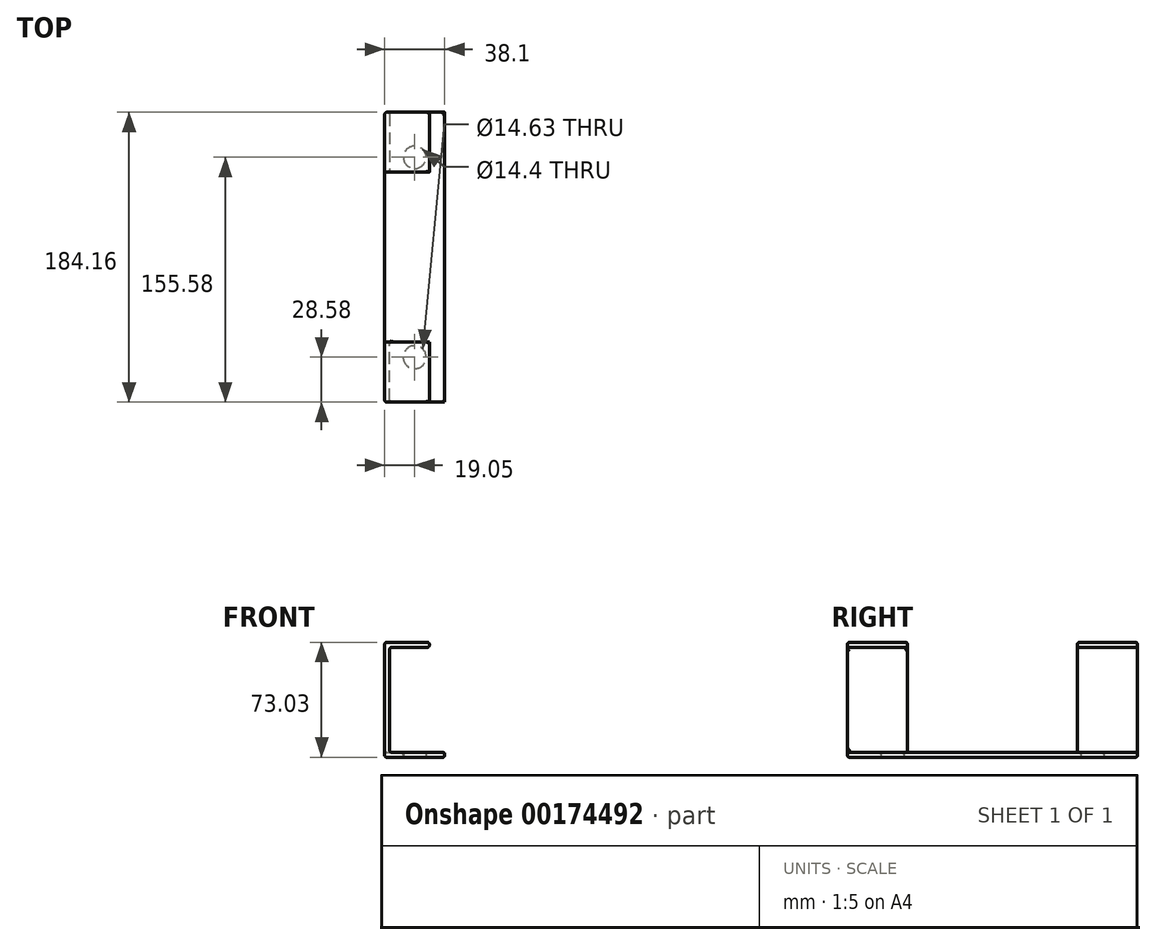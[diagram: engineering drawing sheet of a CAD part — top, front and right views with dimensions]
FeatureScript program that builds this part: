
annotation { "Feature Type Name" : "Feature", "Feature Type Description" : "" }
export const myFeature = defineFeature(function(context is Context, id is Id, definition is map)
    precondition{}
    {
        {
            var Q0;
            Q0=qCreatedBy(makeId("Top.planeOp"),FACE);
            var sketch = newSketch(context, id + "F0", { "sketchPlane" : qUnion([Q0])});
            skLineSegment(sketch, "E0.bottom", {"start": v(-19.05, -92.07) * mm, "end": v(19.05, -92.07) * mm});
            skLineSegment(sketch, "E0.top", {"start": v(-19.05, 92.08) * mm, "end": v(19.05, 92.08) * mm});
            skLineSegment(sketch, "E0.left", {"start": v(-19.05, -92.07) * mm, "end": v(-19.05, 92.08) * mm});
            skLineSegment(sketch, "E0.right", {"start": v(19.05, -92.07) * mm, "end": v(19.05, 92.08) * mm});
            skPoint(sketch, "E0.middle", {"position": v(0, 0) * mm});
            skCircle(sketch, "E1", {"center": v(0, -63.5) * mm, "radius": 7.32 * mm});
            skCircle(sketch, "E2", {"center": v(0, 63.5) * mm, "radius": 7.2 * mm});
            skSolve(sketch);
        }
        {
            var Q0;
            Q0=qSketchRegion(id+"F0",true);
            extrude(context, id + "F1", {"entities" : qUnion([Q0]), "depth" : 3.17 * mm});
        }
        {
            var Q0;
            Q0=qCreatedBy(makeId("Top.planeOp"),FACE);
            cPlane(context, id + "F2", {"entities" : qUnion([Q0]), "cplaneType" : CPlaneType.OFFSET, "offset" : 3.17 * mm, "width" : 152.4 * mm, "height" : 152.4 * mm});
        }
        {
            var Q0;
            Q0=qCreatedBy(id+"F2.planeOp",FACE);
            var sketch = newSketch(context, id + "F3", { "sketchPlane" : qUnion([Q0])});
            skLineSegment(sketch, "E3.bottom", {"start": v(-19.05, 92.08) * mm, "end": v(-15.88, 92.08) * mm});
            skLineSegment(sketch, "E3.top", {"start": v(-19.05, 53.98) * mm, "end": v(-15.88, 53.98) * mm});
            skLineSegment(sketch, "E3.left", {"start": v(-19.05, 92.08) * mm, "end": v(-19.05, 53.98) * mm});
            skLineSegment(sketch, "E3.right", {"start": v(-15.88, 92.08) * mm, "end": v(-15.88, 53.98) * mm});
            skLineSegment(sketch, "E4.MirrorCS", {"start": v(-19.05, -53.98) * mm, "end": v(-15.88, -53.98) * mm});
            skLineSegment(sketch, "E5.MirrorCS", {"start": v(-19.05, -92.08) * mm, "end": v(-19.05, -53.98) * mm});
            skLineSegment(sketch, "E6.MirrorCS", {"start": v(-15.88, -92.08) * mm, "end": v(-15.88, -53.98) * mm});
            skLineSegment(sketch, "E7.MirrorCS", {"start": v(-19.05, -92.08) * mm, "end": v(-15.88, -92.08) * mm});
            skSolve(sketch);
        }
        {
            var Q0;
            Q0=qSketchRegion(id+"F3",true);
            extrude(context, id + "F4", {"entities" : qUnion([Q0]), "operationType" : NewBodyOperationType.ADD, "depth" : 69.85 * mm});
        }
        {
            var Q0;
            Q0=qCreatedBy(makeId("Right.planeOp"),FACE);
            cPlane(context, id + "F5", {"entities" : qUnion([Q0]), "cplaneType" : CPlaneType.OFFSET, "offset" : 16.13 * mm, "oppositeDirection" : true, "width" : 152.4 * mm, "height" : 152.4 * mm});
        }
        {
            var Q0;
            Q0=qCreatedBy(id+"F5.planeOp",FACE);
            var sketch = newSketch(context, id + "F6", { "sketchPlane" : qUnion([Q0])});
            skLineSegment(sketch, "E8.bottom", {"start": v(-92.07, 73.02) * mm, "end": v(-53.97, 73.02) * mm});
            skLineSegment(sketch, "E8.top", {"start": v(-92.07, 69.85) * mm, "end": v(-53.97, 69.85) * mm});
            skLineSegment(sketch, "E8.left", {"start": v(-53.97, 73.02) * mm, "end": v(-53.97, 69.85) * mm});
            skLineSegment(sketch, "E8.right", {"start": v(-92.07, 73.02) * mm, "end": v(-92.07, 69.85) * mm});
            skLineSegment(sketch, "E9.bottom", {"start": v(53.98, 73.03) * mm, "end": v(92.08, 73.03) * mm});
            skLineSegment(sketch, "E9.top", {"start": v(53.98, 69.85) * mm, "end": v(92.08, 69.85) * mm});
            skLineSegment(sketch, "E9.left", {"start": v(53.98, 73.03) * mm, "end": v(53.98, 69.85) * mm});
            skLineSegment(sketch, "E9.right", {"start": v(92.08, 73.03) * mm, "end": v(92.08, 69.85) * mm});
            skSolve(sketch);
        }
        {
            var Q0;
            Q0=qSketchRegion(id+"F6",true);
            extrude(context, id + "F7", {"entities" : qUnion([Q0]), "operationType" : NewBodyOperationType.ADD, "depth" : 25.4 * mm});
        }
        {
            var Q0;
            Q0=makeQuery(id+"F4.opExtrude","CAP_EDGE",EDGE,{"disambiguationData":[OSD([sQuery(id+"F3.wireOp",EDGE,"E3.right")])],"isStart":true});
            var Q1;
            Q1=makeQuery(id+"F4.opExtrude","SWEPT_FACE",FACE,{"disambiguationData":[OSD([sQuery(id+"F3.wireOp",EDGE,"E3.right")])]});
            var Q2;
            Q2=makeQuery(id+"F1.opExtrude","CAP_FACE",FACE,{"disambiguationData":[OSD([sQuery(id+"F0.wireOp",EDGE,"E0.bottom"),sQuery(id+"F0.wireOp",EDGE,"E0.top"),sQuery(id+"F0.wireOp",EDGE,"E0.left"),sQuery(id+"F0.wireOp",EDGE,"E0.right"),sQuery(id+"F0.wireOp",EDGE,"E1"),sQuery(id+"F0.wireOp",EDGE,"E2")])],"isStart":true});
            var Q3;
            Q3=makeQuery(id+"F7.opExtrude","SWEPT_FACE",FACE,{"disambiguationData":[OSD([sQuery(id+"F6.wireOp",EDGE,"E9.top")])]});
            var Q4;
            Q4=makeQuery(id+"F7.opExtrude","SWEPT_FACE",FACE,{"disambiguationData":[OSD([sQuery(id+"F6.wireOp",EDGE,"E8.top")])]});
            var Q5;
            Q5=makeQuery(id+"F7.boolean.opBoolean","MERGE",FACE,{"derivedFrom":[makeQuery(id+"F4.opExtrude","CAP_FACE",FACE,{"disambiguationData":[OSD([sQuery(id+"F3.wireOp",EDGE,"E4.MirrorCS"),sQuery(id+"F3.wireOp",EDGE,"E5.MirrorCS"),sQuery(id+"F3.wireOp",EDGE,"E6.MirrorCS"),sQuery(id+"F3.wireOp",EDGE,"E7.MirrorCS")])],"isStart":false}),makeQuery(id+"F7.opExtrude","SWEPT_FACE",FACE,{"disambiguationData":[OSD([sQuery(id+"F6.wireOp",EDGE,"E8.bottom")])]})]});
            var Q6;
            Q6=makeQuery(id+"F7.boolean.opBoolean","MERGE",FACE,{"derivedFrom":[makeQuery(id+"F4.opExtrude","CAP_FACE",FACE,{"disambiguationData":[OSD([sQuery(id+"F3.wireOp",EDGE,"E3.bottom"),sQuery(id+"F3.wireOp",EDGE,"E3.top"),sQuery(id+"F3.wireOp",EDGE,"E3.left"),sQuery(id+"F3.wireOp",EDGE,"E3.right")])],"isStart":false}),makeQuery(id+"F7.opExtrude","SWEPT_FACE",FACE,{"disambiguationData":[OSD([sQuery(id+"F6.wireOp",EDGE,"E9.bottom")])]})]});
            var Q7;
            Q7=makeQuery(id+"F1.opExtrude","CAP_FACE",FACE,{"disambiguationData":[OSD([sQuery(id+"F0.wireOp",EDGE,"E0.bottom"),sQuery(id+"F0.wireOp",EDGE,"E0.top"),sQuery(id+"F0.wireOp",EDGE,"E0.left"),sQuery(id+"F0.wireOp",EDGE,"E0.right"),sQuery(id+"F0.wireOp",EDGE,"E1"),sQuery(id+"F0.wireOp",EDGE,"E2")])],"isStart":false});
            var Q8;
            Q8=makeQuery(id+"F4.boolean.opBoolean","MERGE",EDGE,{"derivedFrom":[makeQuery(id+"F1.opExtrude","SWEPT_EDGE",EDGE,{"disambiguationData":[OSD([sQuery(id+"F0.wireOp",EDGE,"E0.bottom"),sQuery(id+"F0.wireOp",EDGE,"E0.left")])]}),makeQuery(id+"F4.opExtrude","SWEPT_EDGE",EDGE,{"disambiguationData":[OSD([sQuery(id+"F3.wireOp",EDGE,"E5.MirrorCS"),sQuery(id+"F3.wireOp",EDGE,"E7.MirrorCS")])]})]});
            var Q9;
            Q9=makeQuery(id+"F4.opExtrude","SWEPT_EDGE",EDGE,{"disambiguationData":[OSD([sQuery(id+"F3.wireOp",EDGE,"E4.MirrorCS"),sQuery(id+"F3.wireOp",EDGE,"E5.MirrorCS")])]});
            var Q10;
            Q10=makeQuery(id+"F4.boolean.opBoolean","MERGE",FACE,{"derivedFrom":[makeQuery(id+"F1.opExtrude","SWEPT_FACE",FACE,{"disambiguationData":[OSD([sQuery(id+"F0.wireOp",EDGE,"E0.left")])]}),makeQuery(id+"F4.opExtrude","SWEPT_FACE",FACE,{"disambiguationData":[OSD([sQuery(id+"F3.wireOp",EDGE,"E3.left")])]}),makeQuery(id+"F4.opExtrude","SWEPT_FACE",FACE,{"disambiguationData":[OSD([sQuery(id+"F3.wireOp",EDGE,"E5.MirrorCS")])]})]});
            fillet(context, id + "F8", {"entities" : qUnion([Q0, Q1, Q2, Q3, Q4, Q5, Q6, Q7, Q8, Q9, Q10]), "radius" : 1.27 * mm, "tangentPropagation" : true, "allowEdgeOverflow" : false});
        }
    });
